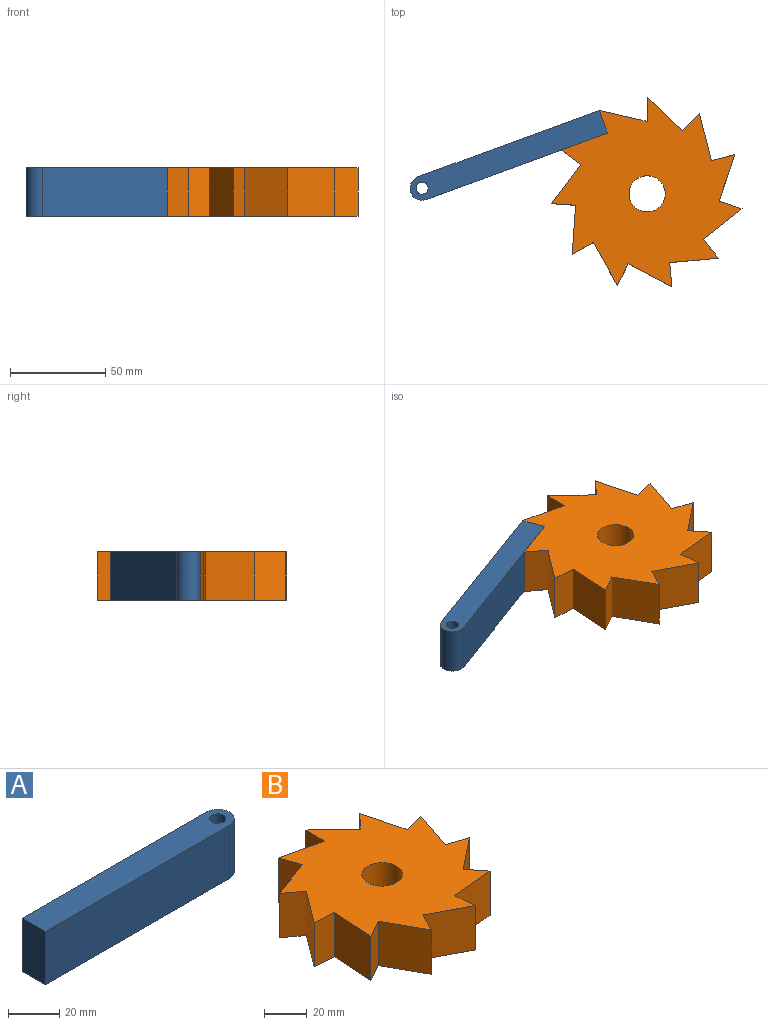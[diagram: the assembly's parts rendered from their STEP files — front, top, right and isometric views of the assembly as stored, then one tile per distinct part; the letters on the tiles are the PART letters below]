
ASSEMBLY  parts=2 mates=1
PART A: 7 faces, bbox 108x12.7x25.4 mm
  f0: plane 101.6x25.4mm, normal (0,-1,0), area 2580.6mm2, adj f1,f3,f5,f6
  f1: cylinder r=6.35mm len=25.4mm, axis (0,0,-1), area 506.7mm2, adj f0,f2,f5,f6
  f2: plane 101.6x25.4mm, normal (0,1,0), area 2580.6mm2, adj f1,f3,f5,f6
  f3: plane 25.4x12.7mm, normal (-1,0,0), area 322.6mm2, adj f0,f2,f5,f6
  f4: cylinder r=3.17mm len=25.4mm, axis (0,0,-1), area 506.7mm2, adj f5,f6
  f5: plane 107.95x12.7mm, normal (0,0,1), area 1322mm2, adj f0,f1,f2,f3,f4
  f6: plane 107.95x12.7mm, normal (0,0,-1), area 1322mm2, adj f0,f1,f2,f3,f4
PART B: 26 faces, bbox 100.2x99.6x25.4 mm
  f0: plane 25.4x12.7mm, normal (-1,0,0), area 322.6mm2, adj f1,f22,f24,f25
  f1: cylinder r=38.1mm len=25.4mm, axis (0,0,-1), area 0.3mm2, adj f0,f2,f24,f25
  f2: plane 25.4x25.13mm, normal (0.22,0.97,0), area 654.8mm2, adj f1,f3,f24,f25
  f3: plane 25.4x11.93mm, normal (-0.94,-0.34,0), area 322.6mm2, adj f2,f4,f24,f25
  f4: plane 25.4x24.21mm, normal (-0.34,0.94,0), area 654.8mm2, adj f3,f5,f24,f25
  f5: plane 25.4x10.16mm, normal (-0.6,-0.8,0), area 322.6mm2, adj f4,f6,f24,f25
  f6: plane 25.4x20.62mm, normal (-0.8,0.6,0), area 654.8mm2, adj f5,f7,f24,f25
  f7: plane 25.4x12.67mm, normal (-0.07,-1,0), area 322.6mm2, adj f6,f8,f24,f25
  f8: plane 25.72x25.4mm, normal (-1,0.07,0), area 654.8mm2, adj f7,f9,f24,f25
  f9: plane 25.4x11.09mm, normal (0.49,-0.87,0), area 322.6mm2, adj f8,f10,f24,f25
  f10: plane 25.4x22.51mm, normal (-0.87,-0.49,0), area 654.8mm2, adj f9,f11,f24,f25
  f11: plane 25.4x11.23mm, normal (0.88,-0.47,0), area 322.6mm2, adj f10,f12,f24,f25
  f12: plane 25.4x22.81mm, normal (-0.47,-0.88,0), area 654.8mm2, adj f11,f13,f24,f25
  f13: plane 25.4x12.65mm, normal (1,0.09,0), area 322.6mm2, adj f12,f14,f24,f25
  f14: plane 25.67x25.4mm, normal (0.09,-1,0), area 654.8mm2, adj f13,f15,f24,f25
  f15: plane 25.4x9.97mm, normal (0.79,0.62,0), area 322.6mm2, adj f14,f16,f24,f25
  f16: plane 25.4x20.25mm, normal (0.62,-0.79,0), area 654.8mm2, adj f15,f17,f24,f25
  f17: plane 25.4x12.03mm, normal (0.32,0.95,0), area 322.6mm2, adj f16,f18,f24,f25
  f18: plane 25.4x24.42mm, normal (0.95,-0.32,0), area 654.8mm2, adj f17,f19,f24,f25
  f19: plane 25.4x12.3mm, normal (-0.25,0.97,0), area 322.6mm2, adj f18,f20,f24,f25
  f20: plane 25.4x24.97mm, normal (0.97,0.25,0), area 654.8mm2, adj f19,f21,f24,f25
  f21: plane 25.4x9.26mm, normal (-0.73,0.68,0), area 322.6mm2, adj f20,f22,f24,f25
  f22: plane 25.4x18.79mm, normal (0.68,0.73,0), area 654.8mm2, adj f0,f21,f24,f25
  f23: cylinder r=9.53mm len=25.4mm, axis (0,0,-1), area 1520.1mm2, adj f24,f25
  f24: plane 100.23x99.65mm, normal (0,0,1), area 5523.5mm2, adj f0,f1,f2,f3,f4,f5,f6,f7
  f25: plane 100.23x99.65mm, normal (0,0,-1), area 5523.5mm2, adj f0,f1,f2,f3,f4,f5,f6,f7
PLACE A rot(axis=(0,0,-1),159.9deg) t=(-79.48,44.62,-11.52)mm
PLACE B t=(-8.82,24.18,1.18)mm
MATE fastened A.f3 <-> B.f3  axis (0.94,0.34,0) through (-31.77,62.08,1.18)mm
